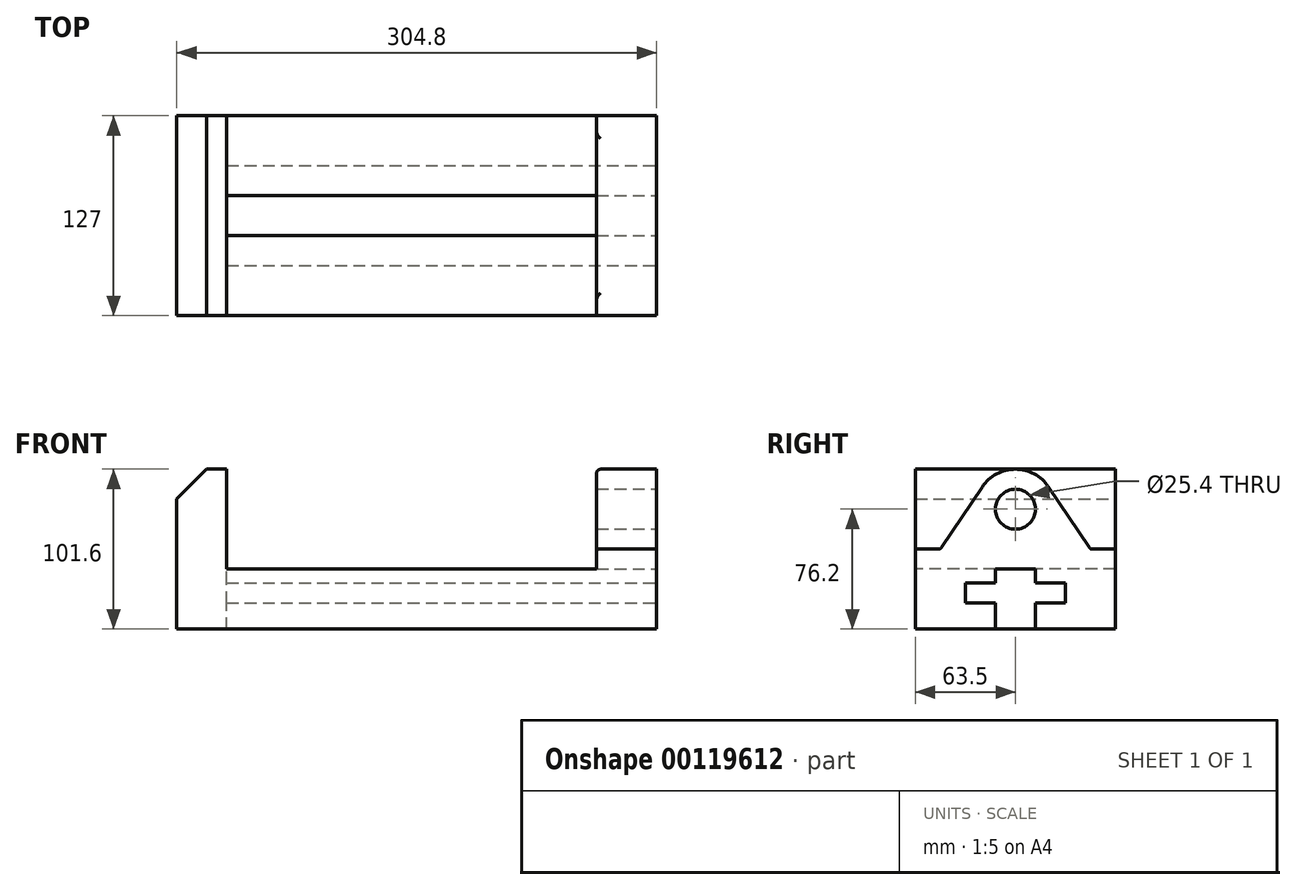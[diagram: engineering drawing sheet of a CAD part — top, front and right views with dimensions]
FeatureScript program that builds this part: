
annotation { "Feature Type Name" : "Feature", "Feature Type Description" : "" }
export const myFeature = defineFeature(function(context is Context, id is Id, definition is map)
    precondition{}
    {
        {
            var Q0;
            Q0=qCreatedBy(makeId("Right.planeOp"),FACE);
            var sketch = newSketch(context, id + "F0", { "sketchPlane" : qUnion([Q0])});
            skLineSegment(sketch, "E0.bottom", {"start": v(0, 0) * mm, "end": v(127, 0) * mm});
            skLineSegment(sketch, "E0.top", {"start": v(0, 101.6) * mm, "end": v(127, 101.6) * mm});
            skLineSegment(sketch, "E0.left", {"start": v(0, 0) * mm, "end": v(0, 101.6) * mm});
            skLineSegment(sketch, "E0.right", {"start": v(127, 0) * mm, "end": v(127, 101.6) * mm});
            skSolve(sketch);
        }
        {
            var Q0;
            Q0=makeQuery(id+"F0.imprint","IMPRINT",FACE,{"disambiguationData":[TD([[makeQuery(id+"F0.imprint","IMPRINT",EDGE,{"derivedFrom":sQuery(id+"F0.wireOp",EDGE,"E0.bottom")}),1.0]])]});
            extrude(context, id + "F1", {"entities" : qUnion([Q0]), "oppositeDirection" : true, "depth" : 304.8 * mm});
        }
        {
            var Q0;
            Q0=makeQuery(id+"F1.opExtrude","SWEPT_FACE",FACE,{"disambiguationData":[OSD([sQuery(id+"F0.wireOp",EDGE,"E0.left")])]});
            var sketch = newSketch(context, id + "F2", { "sketchPlane" : qUnion([Q0])});
            skLineSegment(sketch, "E1.bottom", {"start": v(-273.05, 101.6) * mm, "end": v(-38.1, 101.6) * mm});
            skLineSegment(sketch, "E1.top", {"start": v(-273.05, 38.1) * mm, "end": v(-38.1, 38.1) * mm});
            skLineSegment(sketch, "E1.left", {"start": v(-273.05, 101.6) * mm, "end": v(-273.05, 38.1) * mm});
            skLineSegment(sketch, "E1.right", {"start": v(-38.1, 101.6) * mm, "end": v(-38.1, 38.1) * mm});
            skSolve(sketch);
        }
        {
            var Q0;
            Q0=makeQuery(id+"F2.imprint","IMPRINT",FACE,{"disambiguationData":[TD([[makeQuery(id+"F2.imprint","IMPRINT",EDGE,{"derivedFrom":sQuery(id+"F2.wireOp",EDGE,"E1.bottom")}),-1.0]])]});
            extrude(context, id + "F3", {"entities" : qUnion([Q0]), "operationType" : NewBodyOperationType.REMOVE, "endBound" : BoundingType.THROUGH_ALL, "oppositeDirection" : true, "depth" : 25.4 * mm});
        }
        {
            var Q0;
            Q0=makeQuery(id+"F1.opExtrude","CAP_FACE",FACE,{"disambiguationData":[OSD([sQuery(id+"F0.wireOp",EDGE,"E0.bottom"),sQuery(id+"F0.wireOp",EDGE,"E0.top"),sQuery(id+"F0.wireOp",EDGE,"E0.left"),sQuery(id+"F0.wireOp",EDGE,"E0.right")])],"isStart":true});
            var sketch = newSketch(context, id + "F4", { "sketchPlane" : qUnion([Q0])});
            skLineSegment(sketch, "E2", {"start": v(0, 50.8) * mm, "end": v(15.87, 50.8) * mm});
            skLineSegment(sketch, "E3", {"start": v(15.87, 50.8) * mm, "end": v(42.4, 90.35) * mm});
            skArc(sketch, "E4", {"start": v(84.6, 90.35) * mm, "mid": v(63.5, 101.6) * mm, "end": v(42.4, 90.35) * mm});
            skLineSegment(sketch, "E5", {"start": v(84.6, 90.35) * mm, "end": v(111.12, 50.8) * mm});
            skLineSegment(sketch, "E6", {"start": v(111.12, 50.8) * mm, "end": v(127, 50.8) * mm});
            skLineSegment(sketch, "E7", {"start": v(0, 76.2) * mm, "end": v(127, 76.2) * mm, "construction": true});
            skCircle(sketch, "E8", {"center": v(63.5, 76.2) * mm, "radius": 12.7 * mm});
            skLineSegment(sketch, "E9", {"start": v(63.5, 101.6) * mm, "end": v(63.5, 0) * mm, "construction": true});
            skLineSegment(sketch, "E10.bottom", {"start": v(50.8, 0) * mm, "end": v(76.2, 0) * mm});
            skLineSegment(sketch, "E10.top", {"start": v(50.8, 38.1) * mm, "end": v(76.2, 38.1) * mm});
            skLineSegment(sketch, "E10.left", {"start": v(50.8, 0) * mm, "end": v(50.8, 16.51) * mm});
            skLineSegment(sketch, "E10.right", {"start": v(76.2, 0) * mm, "end": v(76.2, 16.51) * mm});
            skPoint(sketch, "E10.middle", {"position": v(63.5, 19.05) * mm});
            skLineSegment(sketch, "E11.bottom", {"start": v(31.75, 16.51) * mm, "end": v(50.8, 16.51) * mm});
            skLineSegment(sketch, "E11.top", {"start": v(31.75, 29.21) * mm, "end": v(50.8, 29.21) * mm});
            skLineSegment(sketch, "E11.left", {"start": v(31.75, 16.51) * mm, "end": v(31.75, 29.21) * mm});
            skLineSegment(sketch, "E11.right", {"start": v(95.25, 16.51) * mm, "end": v(95.25, 29.21) * mm});
            skPoint(sketch, "E11.middle", {"position": v(63.5, 22.86) * mm});
            skLineSegment(sketch, "E12.trimOffspring", {"start": v(50.8, 29.21) * mm, "end": v(50.8, 38.1) * mm});
            skLineSegment(sketch, "E13.trimOffspring", {"start": v(76.2, 29.21) * mm, "end": v(76.2, 38.1) * mm});
            skLineSegment(sketch, "E14.trimOffspring", {"start": v(76.2, 29.21) * mm, "end": v(95.25, 29.21) * mm});
            skLineSegment(sketch, "E15.trimOffspring", {"start": v(76.2, 16.51) * mm, "end": v(95.25, 16.51) * mm});
            skSolve(sketch);
        }
        {
            var Q0;
            Q0=makeQuery(id+"F4.imprint","IMPRINT",FACE,{"disambiguationData":[TD([[makeQuery(id+"F4.imprint","IMPRINT",EDGE,{"derivedFrom":sQuery(id+"F4.wireOp",EDGE,"E8")}),1.0]])]});
            var Q1;
            Q1=makeQuery(id+"F4.imprint","IMPRINT",FACE,{"disambiguationData":[TD([[makeQuery(id+"F4.imprint","IMPRINT",EDGE,{"derivedFrom":sQuery(id+"F4.wireOp",EDGE,"E10.bottom")}),1.0]])]});
            var Q2;
            {var subQ6=sQuery(id+"F4.wireOp",EDGE,"E2");Q2=makeQuery(id+"F4.imprint","IMPRINT",FACE,{"disambiguationData":[TD([[makeQuery(id+"F4.imprint","IMPRINT",EDGE,{"derivedFrom":subQ6}),1.0]])]});}
            var Q3;
            {var subQ6=sQuery(id+"F4.wireOp",EDGE,"E5");Q3=makeQuery(id+"F4.imprint","IMPRINT",FACE,{"disambiguationData":[TD([[makeQuery(id+"F4.imprint","IMPRINT",EDGE,{"derivedFrom":subQ6}),1.0]])]});}
            var Q4;
            Q4=makeQuery(id+"F3.boolean.opBoolean","COPY",FACE,{"derivedFrom":makeQuery(id+"F3.opExtrude","SWEPT_FACE",FACE,{"disambiguationData":[OSD([sQuery(id+"F2.wireOp",EDGE,"E1.left")])]})});
            extrude(context, id + "F5", {"entities" : qUnion([Q0, Q1, Q2, Q3]), "operationType" : NewBodyOperationType.REMOVE, "endBound" : BoundingType.UP_TO_SURFACE, "oppositeDirection" : true, "endBoundEntityFace" : qUnion([Q4]), "depth" : 25.4 * mm});
        }
        {
            var Q0;
            Q0=makeQuery(id+"F1.opExtrude","CAP_EDGE",EDGE,{"disambiguationData":[OSD([sQuery(id+"F0.wireOp",EDGE,"E0.top")])],"isStart":false});
            chamfer(context, id + "F6", {"entities" : qUnion([Q0]), "width" : 19.05 * mm, "tangentPropagation" : true});
        }
        {
            var Q0;
            Q0=makeQuery(id+"F5.boolean.opBoolean","COPY",EDGE,{"derivedFrom":makeQuery(id+"F5.opExtrude","SWEPT_EDGE",EDGE,{"disambiguationData":[OSD([sQuery(id+"F4.wireOp",EDGE,"E2"),sQuery(id+"F4.wireOp",EDGE,"E3")])]})});
            var Q1;
            Q1=makeQuery(id+"F5.boolean.opBoolean","COPY",EDGE,{"derivedFrom":makeQuery(id+"F5.opExtrude","CAP_EDGE",EDGE,{"disambiguationData":[OSD([sQuery(id+"F4.wireOp",EDGE,"E3")])],"isStart":true})});
            var Q2;
            Q2=makeQuery(id+"F5.boolean.opBoolean","INTERSECT",EDGE,{"derivedFrom":[makeQuery(id+"F3.boolean.opBoolean","COPY",FACE,{"derivedFrom":makeQuery(id+"F3.opExtrude","SWEPT_FACE",FACE,{"disambiguationData":[OSD([sQuery(id+"F2.wireOp",EDGE,"E1.right")])]})}),makeQuery(id+"F5.opExtrude","SWEPT_FACE",FACE,{"disambiguationData":[OSD([sQuery(id+"F4.wireOp",EDGE,"E3")])]})]});
            var Q3;
            Q3=makeQuery(id+"F5.boolean.opBoolean","COPY",EDGE,{"derivedFrom":makeQuery(id+"F5.opExtrude","SWEPT_EDGE",EDGE,{"disambiguationData":[OSD([sQuery(id+"F4.wireOp",EDGE,"E5"),sQuery(id+"F4.wireOp",EDGE,"E6")])]})});
            var Q4;
            Q4=makeQuery(id+"F5.boolean.opBoolean","COPY",EDGE,{"derivedFrom":makeQuery(id+"F5.opExtrude","SWEPT_EDGE",EDGE,{"disambiguationData":[OSD([sQuery(id+"F0.wireOp",EDGE,"E0.right"),sQuery(id+"F4.wireOp",EDGE,"E6")])]})});
            var Q5;
            Q5=makeQuery(id+"F5.boolean.opBoolean","COPY",EDGE,{"derivedFrom":makeQuery(id+"F5.opExtrude","SWEPT_EDGE",EDGE,{"disambiguationData":[OSD([sQuery(id+"F0.wireOp",EDGE,"E0.left"),sQuery(id+"F4.wireOp",EDGE,"E2")])]})});
            fillet(context, id + "F7", {"entities" : qUnion([Q0, Q1, Q2, Q3, Q4, Q5]), "radius" : 2.54 * mm, "tangentPropagation" : true, "allowEdgeOverflow" : false});
        }
    });
